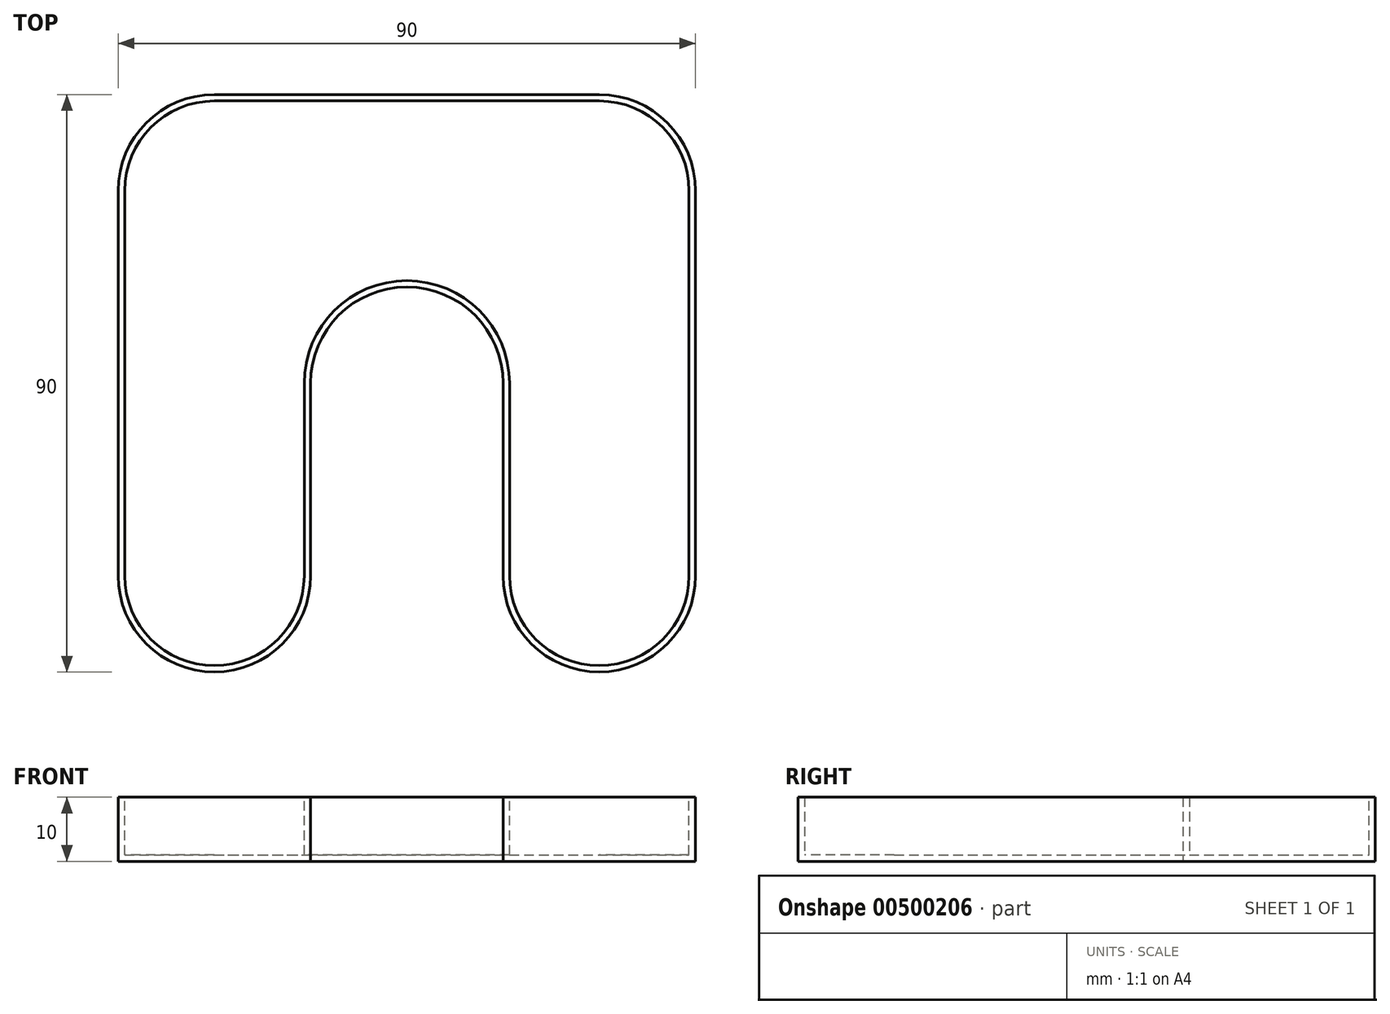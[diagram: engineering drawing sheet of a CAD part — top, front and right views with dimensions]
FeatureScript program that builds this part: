
annotation { "Feature Type Name" : "Feature", "Feature Type Description" : "" }
export const myFeature = defineFeature(function(context is Context, id is Id, definition is map)
    precondition{}
    {
        {
            var Q0;
            Q0=qCreatedBy(makeId("Top.planeOp"),FACE);
            var sketch = newSketch(context, id + "F0", { "sketchPlane" : qUnion([Q0])});
            skLineSegment(sketch, "E0.bottom", {"start": v(15, 0) * mm, "end": v(15, 0) * mm});
            skLineSegment(sketch, "E0.top", {"start": v(15, 90) * mm, "end": v(75, 90) * mm});
            skLineSegment(sketch, "E0.left", {"start": v(0, 15) * mm, "end": v(0, 75) * mm});
            skLineSegment(sketch, "E0.right", {"start": v(90, 15) * mm, "end": v(90, 75) * mm});
            skLineSegment(sketch, "E1", {"start": v(60, 15) * mm, "end": v(60, 45) * mm});
            skLineSegment(sketch, "E2", {"start": v(30, 15) * mm, "end": v(30, 45) * mm});
            skLineSegment(sketch, "E3", {"start": v(45, 60) * mm, "end": v(45, 60) * mm});
            skLineSegment(sketch, "E4.trimOffspring", {"start": v(75, 0) * mm, "end": v(75, 0) * mm});
            skPoint(sketch, "E5.visualSharp", {"position": v(0, 90) * mm});
            skArc(sketch, "E5.filletArc", {"start": v(15, 90) * mm, "mid": v(4.4, 85.6) * mm, "end": v(0, 75) * mm});
            skPoint(sketch, "E6.visualSharp", {"position": v(0, 0) * mm});
            skArc(sketch, "E6.filletArc", {"start": v(0, 15) * mm, "mid": v(4.4, 4.4) * mm, "end": v(15, 0) * mm});
            skPoint(sketch, "E7.visualSharp", {"position": v(90, 90) * mm});
            skArc(sketch, "E7.filletArc", {"start": v(90, 75) * mm, "mid": v(85.6, 85.6) * mm, "end": v(75, 90) * mm});
            skPoint(sketch, "E8.visualSharp", {"position": v(60, 0) * mm});
            skArc(sketch, "E8.filletArc", {"start": v(60, 15) * mm, "mid": v(64.4, 4.4) * mm, "end": v(75, 0) * mm});
            skPoint(sketch, "E9.visualSharp", {"position": v(30, 0) * mm});
            skArc(sketch, "E9.filletArc", {"start": v(15, 0) * mm, "mid": v(25.6, 4.4) * mm, "end": v(30, 15) * mm});
            skPoint(sketch, "E10.visualSharp", {"position": v(90, 0) * mm});
            skArc(sketch, "E10.filletArc", {"start": v(75, 0) * mm, "mid": v(85.6, 4.4) * mm, "end": v(90, 15) * mm});
            skPoint(sketch, "E11.visualSharp", {"position": v(30, 60) * mm});
            skArc(sketch, "E11.filletArc", {"start": v(45, 60) * mm, "mid": v(34.4, 55.6) * mm, "end": v(30, 45) * mm});
            skPoint(sketch, "E12.visualSharp", {"position": v(60, 60) * mm});
            skArc(sketch, "E12.filletArc", {"start": v(60, 45) * mm, "mid": v(55.6, 55.6) * mm, "end": v(45, 60) * mm});
            skSolve(sketch);
        }
        {
            var Q0;
            Q0 = qSketchRegion(id + "F0", true);
            extrude(context, id + "F1", {"entities" : qUnion([Q0]), "depth" : 10 * mm});
        }
        {
            var Q0;
            Q0=makeQuery(id+"F1.opExtrude","CAP_FACE",FACE,{"disambiguationData":[OSD([sQuery(id+"F0.wireOp",EDGE,"E0.top"),sQuery(id+"F0.wireOp",EDGE,"E0.left"),sQuery(id+"F0.wireOp",EDGE,"E0.right"),sQuery(id+"F0.wireOp",EDGE,"E1"),sQuery(id+"F0.wireOp",EDGE,"E2"),sQuery(id+"F0.wireOp",EDGE,"E5.filletArc"),sQuery(id+"F0.wireOp",EDGE,"E6.filletArc"),sQuery(id+"F0.wireOp",EDGE,"E7.filletArc"),sQuery(id+"F0.wireOp",EDGE,"E8.filletArc"),sQuery(id+"F0.wireOp",EDGE,"E9.filletArc"),sQuery(id+"F0.wireOp",EDGE,"E10.filletArc"),sQuery(id+"F0.wireOp",EDGE,"E11.filletArc"),sQuery(id+"F0.wireOp",EDGE,"E12.filletArc")])],"isStart":false});
            shell(context, id + "F2", {"entities" : qUnion([Q0]), "thickness" : 1 * mm});
        }
    });
